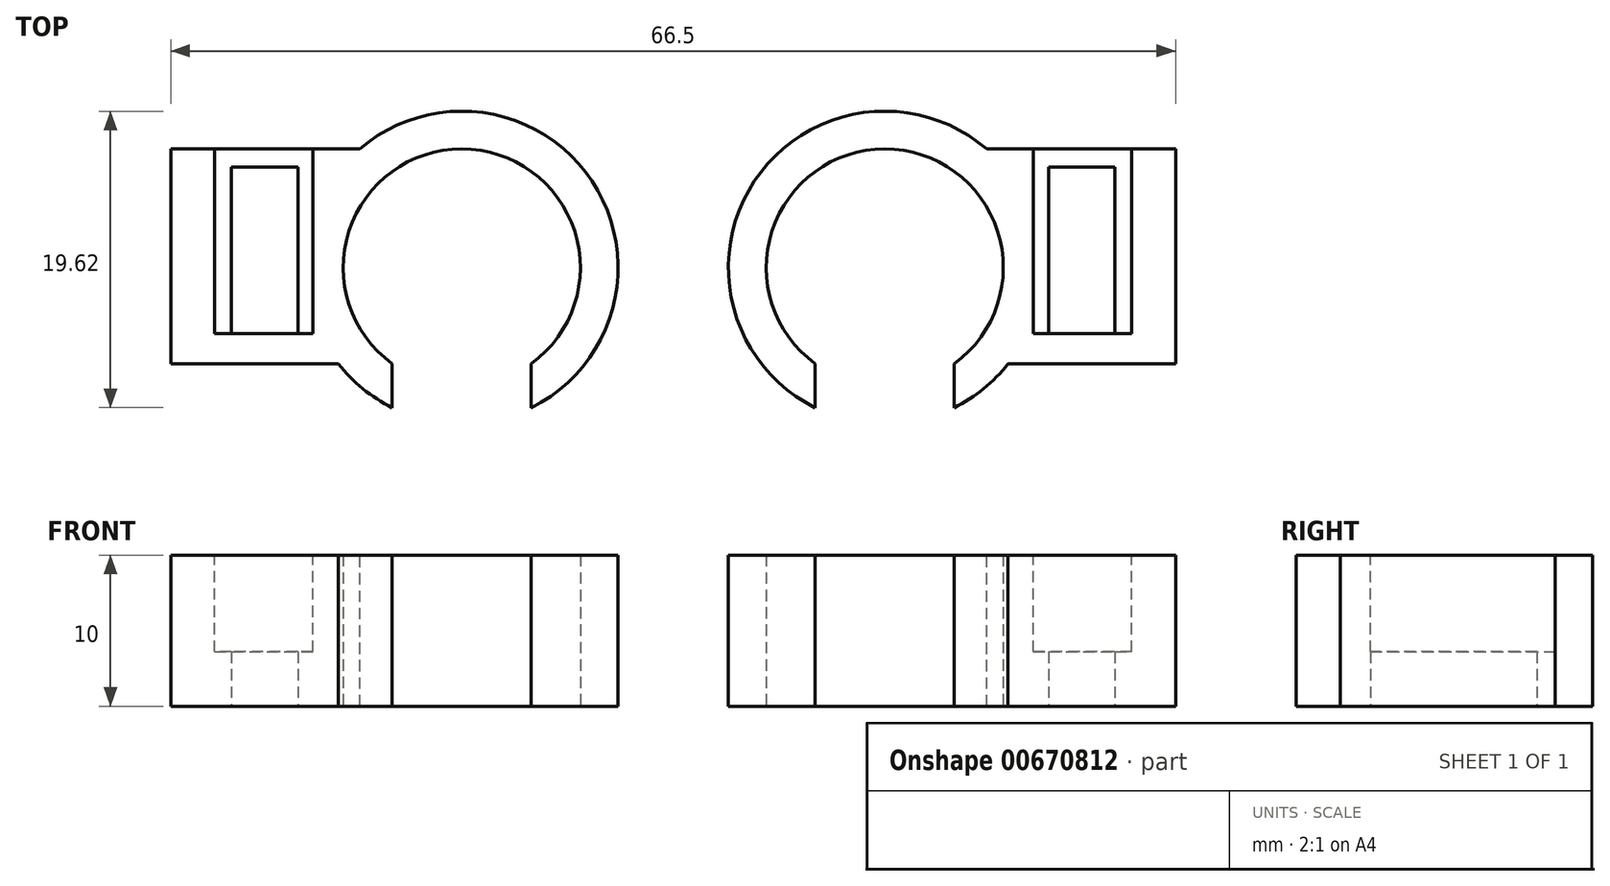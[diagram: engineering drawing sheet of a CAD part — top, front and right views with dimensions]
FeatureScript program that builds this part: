
annotation { "Feature Type Name" : "Feature", "Feature Type Description" : "" }
export const myFeature = defineFeature(function(context is Context, id is Id, definition is map)
    precondition{}
    {
        {
            var Q0;
            Q0=qCreatedBy(makeId("Top.planeOp"),FACE);
            var sketch = newSketch(context, id + "F0", { "sketchPlane" : qUnion([Q0])});
            skCircle(sketch, "E0", {"center": v(0, 0) * mm, "radius": 10.35 * mm});
            skCircle(sketch, "E1", {"center": v(0, 0) * mm, "radius": 7.85 * mm});
            skSolve(sketch);
        }
        {
            var Q0;
            Q0=makeQuery(id+"F0.imprint","IMPRINT",FACE,{"disambiguationData":[TD([[makeQuery(id+"F0.imprint","IMPRINT",EDGE,{"derivedFrom":sQuery(id+"F0.wireOp",EDGE,"E0")}),1.0]])]});
            extrude(context, id + "F1", {"entities" : qUnion([Q0]), "depth" : 10 * mm, "offsetDistance" : 25 * mm});
        }
        {
            var Q0;
            Q0=makeQuery(id+"F1.opExtrude","CAP_FACE",FACE,{"disambiguationData":[OSD([sQuery(id+"F0.wireOp",EDGE,"E0"),sQuery(id+"F0.wireOp",EDGE,"E1")])],"isStart":false});
            var sketch = newSketch(context, id + "F2", { "sketchPlane" : qUnion([Q0])});
            skLineSegment(sketch, "E2.bottom", {"start": v(-4.6, -6.36) * mm, "end": v(4.6, -6.36) * mm});
            skLineSegment(sketch, "E2.top", {"start": v(-4.6, -10.93) * mm, "end": v(4.6, -10.93) * mm});
            skLineSegment(sketch, "E2.left", {"start": v(-4.6, -6.36) * mm, "end": v(-4.6, -10.93) * mm});
            skLineSegment(sketch, "E2.right", {"start": v(4.6, -6.36) * mm, "end": v(4.6, -10.93) * mm});
            skSolve(sketch);
        }
        {
            var Q0;
            {var subQ0=sQuery(id+"F2.wireOp",EDGE,"E2.left");var subQ4=makeQuery(id+"F1.opExtrude","CAP_EDGE",EDGE,{"disambiguationData":[OSD([sQuery(id+"F0.wireOp",EDGE,"E0")])],"isStart":false});var subQ5=makeQuery(id+"F2.imprint","INTERSECT",VERTEX,{"derivedFrom":[subQ4,subQ0]});Q0=makeQuery(id+"F2.imprint","IMPRINT",FACE,{"disambiguationData":[TD([[makeQuery(id+"F2.imprint","IMPRINT",EDGE,{"disambiguationData":[TD([[subQ5,-1.0]])],"derivedFrom":subQ4}),1.0]])]});}
            extrude(context, id + "F3", {"entities" : qUnion([Q0]), "operationType" : NewBodyOperationType.REMOVE, "oppositeDirection" : true, "depth" : 25 * mm, "offsetDistance" : 25 * mm});
        }
        {
            var Q0;
            Q0=makeQuery(id+"F1.opExtrude","CAP_FACE",FACE,{"disambiguationData":[OSD([sQuery(id+"F0.wireOp",EDGE,"E0"),sQuery(id+"F0.wireOp",EDGE,"E1")])],"isStart":false});
            var sketch = newSketch(context, id + "F4", { "sketchPlane" : qUnion([Q0])});
            skLineSegment(sketch, "E3", {"start": v(-6.75, 7.85) * mm, "end": v(-19.25, 7.85) * mm});
            skPoint(sketch, "E3.startSnap0", {"position": v(0, 7.85) * mm});
            skLineSegment(sketch, "E4", {"start": v(-19.25, 7.85) * mm, "end": v(-19.25, -6.36) * mm});
            skLineSegment(sketch, "E5", {"start": v(-19.25, -6.36) * mm, "end": v(-4.6, -6.36) * mm});
            skSolve(sketch);
        }
        {
            var Q0;
            {var subQ0=sQuery(id+"F4.wireOp",EDGE,"E3");Q0=makeQuery(id+"F4.imprint","IMPRINT",FACE,{"disambiguationData":[TD([[makeQuery(id+"F4.imprint","IMPRINT",EDGE,{"derivedFrom":subQ0}),1.0]])]});}
            var Q1;
            Q1=makeQuery(id+"F1.opExtrude","CAP_FACE",FACE,{"disambiguationData":[OSD([sQuery(id+"F0.wireOp",EDGE,"E0"),sQuery(id+"F0.wireOp",EDGE,"E1")])],"isStart":true});
            extrude(context, id + "F5", {"entities" : qUnion([Q0]), "operationType" : NewBodyOperationType.ADD, "endBound" : BoundingType.UP_TO_SURFACE, "oppositeDirection" : true, "depth" : 25 * mm, "endBoundEntityFace" : qUnion([Q1]), "offsetDistance" : 25 * mm});
        }
        {
            var Q0;
            {var subQ0=sQuery(id+"F0.wireOp",EDGE,"E0");Q0=makeQuery(id+"F5.boolean.opBoolean","MERGE",FACE,{"derivedFrom":[makeQuery(id+"F1.opExtrude","CAP_FACE",FACE,{"disambiguationData":[OSD([subQ0,sQuery(id+"F0.wireOp",EDGE,"E1")])],"isStart":false}),makeQuery(id+"F5.opExtrude","CAP_FACE",FACE,{"disambiguationData":[OSD([subQ0,sQuery(id+"F4.wireOp",EDGE,"E3"),sQuery(id+"F4.wireOp",EDGE,"E4"),sQuery(id+"F4.wireOp",EDGE,"E5")])],"isStart":true})]});}
            var sketch = newSketch(context, id + "F6", { "sketchPlane" : qUnion([Q0])});
            skLineSegment(sketch, "E6.0", {"start": v(-16.35, -4.36) * mm, "end": v(-9.85, -4.36) * mm});
            skLineSegment(sketch, "E6.1", {"start": v(-16.35, 8.5) * mm, "end": v(-16.35, -4.36) * mm});
            skLineSegment(sketch, "E7", {"start": v(-9.85, 8.5) * mm, "end": v(-9.85, -4.36) * mm});
            skLineSegment(sketch, "E8", {"start": v(-16.35, 8.5) * mm, "end": v(-9.85, 8.5) * mm});
            skSolve(sketch);
        }
        {
            var Q0;
            Q0 = qSketchRegion(id + "F6", true);
            var Q1;
            {var subQ0=sQuery(id+"F0.wireOp",EDGE,"E1");var subQ1=sQuery(id+"F0.wireOp",EDGE,"E0");Q1=makeQuery(id+"F5.boolean.opBoolean","MERGE",FACE,{"derivedFrom":[makeQuery(id+"F1.opExtrude","CAP_FACE",FACE,{"disambiguationData":[OSD([subQ1,subQ0])],"isStart":true}),makeQuery(id+"F5.opExtrude","CAP_FACE",FACE,{"disambiguationData":[OSD([subQ1,subQ0])],"isStart":false})]});}
            extrude(context, id + "F7", {"entities" : qUnion([Q0]), "operationType" : NewBodyOperationType.REMOVE, "endBound" : BoundingType.UP_TO_SURFACE, "oppositeDirection" : true, "depth" : 25 * mm, "endBoundEntityFace" : qUnion([Q1]), "hasOffset" : true, "offsetDistance" : (10 - 6.4) * mm});
        }
        {
            var Q0;
            {var subQ0=sQuery(id+"F0.wireOp",EDGE,"E1");var subQ1=sQuery(id+"F0.wireOp",EDGE,"E0");Q0=makeQuery(id+"F5.boolean.opBoolean","MERGE",FACE,{"derivedFrom":[makeQuery(id+"F1.opExtrude","CAP_FACE",FACE,{"disambiguationData":[OSD([subQ1,subQ0])],"isStart":true}),makeQuery(id+"F5.opExtrude","CAP_FACE",FACE,{"disambiguationData":[OSD([subQ1,subQ0])],"isStart":false})]});}
            var sketch = newSketch(context, id + "F8", { "sketchPlane" : qUnion([Q0])});
            skLineSegment(sketch, "E9.0", {"start": v(-15.25, -6.65) * mm, "end": v(-10.85, -6.65) * mm});
            skLineSegment(sketch, "E9.1", {"start": v(-15.25, 4.36) * mm, "end": v(-15.25, -6.65) * mm});
            skLineSegment(sketch, "E9.2", {"start": v(-10.85, 4.36) * mm, "end": v(-15.25, 4.36) * mm});
            skLineSegment(sketch, "E10", {"start": v(-10.85, 4.36) * mm, "end": v(-10.85, -6.65) * mm});
            skSolve(sketch);
        }
        {
            var Q0;
            Q0=makeQuery(id+"F8.imprint","IMPRINT",FACE,{"disambiguationData":[TD([[makeQuery(id+"F8.imprint","IMPRINT",EDGE,{"derivedFrom":sQuery(id+"F8.wireOp",EDGE,"E9.0")}),1.0]])]});
            extrude(context, id + "F9", {"entities" : qUnion([Q0]), "operationType" : NewBodyOperationType.REMOVE, "oppositeDirection" : true, "depth" : 25 * mm, "offsetDistance" : 25 * mm});
        }
        {
            var Q0;
            Q0=makeQuery(id+"F1.opExtrude","SWEPT_BODY",BODY,{"disambiguationData":[OSD([sQuery(id+"F0.wireOp",EDGE,"E0"),sQuery(id+"F0.wireOp",EDGE,"E1")])]});
            var Q1;
            Q1=qCreatedBy(makeId("Right.planeOp"),FACE);
            mirror(context, id + "F10", {"entities" : qUnion([Q0]), "mirrorPlane" : qUnion([Q1])});
        }
        {
            var Q0;
            Q0=makeQuery(id+"F10.opPattern","COPY",BODY,{"derivedFrom":makeQuery(id+"F1.opExtrude","SWEPT_BODY",BODY,{"disambiguationData":[OSD([sQuery(id+"F0.wireOp",EDGE,"E0"),sQuery(id+"F0.wireOp",EDGE,"E1")])]}),"instanceName":"1"});
            transform(context, id + "F11", {"entities" : qUnion([Q0]), "transformType" : TransformType.TRANSLATION_3D, "dx" : 31.1 * mm, "dy" : 0 * mm, "dz" : 0 * mm, "makeCopy" : false});
        }
        {
            var Q0;
            Q0=makeQuery(id+"F10.opPattern","COPY",BODY,{"derivedFrom":makeQuery(id+"F1.opExtrude","SWEPT_BODY",BODY,{"disambiguationData":[OSD([sQuery(id+"F0.wireOp",EDGE,"E0"),sQuery(id+"F0.wireOp",EDGE,"E1")])]}),"instanceName":"1"});
            deleteBodies(context, id + "F12", {"entities" : qUnion([Q0])});
        }
        {
            var Q0;
            Q0=makeQuery(id+"F1.opExtrude","SWEPT_BODY",BODY,{"disambiguationData":[OSD([sQuery(id+"F0.wireOp",EDGE,"E0"),sQuery(id+"F0.wireOp",EDGE,"E1")])]});
            var Q1;
            Q1=qCreatedBy(makeId("Right.planeOp"),FACE);
            mirror(context, id + "F13", {"entities" : qUnion([Q0]), "mirrorPlane" : qUnion([Q1])});
        }
        {
            var Q0;
            Q0=makeQuery(id+"F13.opPattern","COPY",BODY,{"derivedFrom":makeQuery(id+"F1.opExtrude","SWEPT_BODY",BODY,{"disambiguationData":[OSD([sQuery(id+"F0.wireOp",EDGE,"E0"),sQuery(id+"F0.wireOp",EDGE,"E1")])]}),"instanceName":"1"});
            transform(context, id + "F14", {"entities" : qUnion([Q0]), "transformType" : TransformType.TRANSLATION_3D, "dx" : 28 * mm, "dy" : 0 * mm, "dz" : 0 * mm, "makeCopy" : false});
        }
    });
